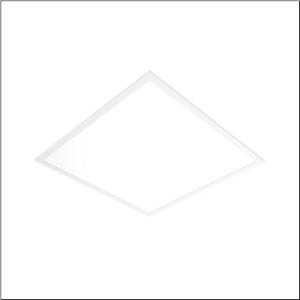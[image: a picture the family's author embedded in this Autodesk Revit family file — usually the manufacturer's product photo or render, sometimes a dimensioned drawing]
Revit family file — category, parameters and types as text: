
# Revit family: apollon_r__41_51mh11wd2443_7c66
name_source: partatom
category: Lighting Fixtures
units: mm (PartAtom-declared; Revit-internal decimal feet)

## family parameters
Cut with Voids When Loaded = No
Host = Face
Light Source = No
Part Type = Normal
Room Calculation Point = No
Round Connector Dimension = Use Diameter
Shared = No

## types (1)
- Apollon® 41 (1 x LED, 3500 lm, 28.5 W, 4000K)
    Apparent Load = 29 VA
    CIE Flux Codes = 61 87 97 100 100
    Color Rendering = 80
    Color Temperature = 4000K
    Default Elevation = 1800 mm
    Description = Apollon® 41, office luminaire, primary optical cover: prismatic diffuser, of PS, light emission: direct distribution, primary light characteristic: symmetric, installation type: lay-in mounting, LED, rated luminous flux: 3.500lm, luminous efficacy: 123lm/W, light colour: 840, colour temperature: 4000K, with terminal, 5-pole, mains connection: 220..240V, AC/DC, 0/50..60Hz, housing, of aluminium section, traffic white (RAL 9016), module: M625, length: 620mm, width: 620mm, height: 28mm, housing upper side, of sheet steel, protection rating (complete): IP20, protection rating (lamp compartment, on room side): IP40, insulation class (complete): insulation class II (safety insulation), certification: CE, ENEC, permissible operating ambient temperature: -25..+40°C, packaging unit: 1 piece
    Height = 0 mm  [stored 0 ft]
    Lamp = 1 x LED
    Lamp Light Flux = 3500 lm
    Lamp Power = 28.5 W
    Lamp count = 1
    Length = 620 mm
    Luminous efficacy = 123 lm/W
    Manufacturer = Siteco
    ModVariant = No
    Model = 51MH11WD2443
    Mounting Place = Ceiling
    Mounting Type = Recessed
    Number of Poles = 1
    OnlyDefault = Yes
    Power Factor = 1
    Product Name = Apollon® 41
    Product group = office luminaire | ceiling recessed
    ProductGroupID = 400
    Protection Class = Protection class II
    Protection Degree = IP 20
    RLX_Detail_Level = 1
    RLX_Emergency_Light_Flux = 0 lm
    RLX_Emergency_Type = 0
    RLX_Emergency_Type_DB = No
    RlxData = <blob elided: 12189 chars, md5=a1518a41>
    Socket = socket
    Standby Power = 0 W
    System Light Flux = 3500 lm
    System Power = 29 W
    Type Comments = Product without accessories
    Type Image = l_1291024.jpg
    URL = http://relux.com
    VarID = ---
    Voltage = 0 V
    Weight = 0.00 kg
    Width = 620 mm

note: [stored X ft] marks values corroborated as IEEE doubles in the binary element streams (Revit-internal decimal feet)

## geometry (parser evidence)
native form markers: Sweep x11
no freeform markers — native parametric forms only
